# Revit family: Walk_in_Door-ELT_Custom_Coolers-Single_Swing-Left_Hinge
name_source: partatom
category: Doors
units: mm (PartAtom-declared; Revit-internal decimal feet)

## family parameters
Always vertical = Yes
Cut with Voids When Loaded = No
Host = Wall
OmniClass Number = 23.30.10.00
OmniClass Title = Doors
Room Calculation Point = No
Shared = No

## types (18) — shared parameters
Analytic Construction = <None>
Define Thermal Properties by = Schematic Type
Frame Material = ELT_White Stucco Embossed
Frame Width = 5 1/2"
Function = Interior
Manufacturer = ELT Custom Coolers
Panel Material = ELT_White Stucco Embossed
Product Page URL = https://eltcoolerdoors.com
Thickness = 4"
URL = https://eltcoolerdoors.com
Wall Closure = By host

## per-type parameters (varying)
| type | Description | Frame Thickness | Height | Jamb Frame | Model | Plug Frame | Rough Height | Rough Width | Width |
| 72" x 84" Cooler, Jamb Frame | Walk in Swing Cooler Door 72"x 84" Prehung with a Retrofit Heated & Jamb Frame for New Construction. Left Hinge | 1 1/2" | 84" | Yes | ELT 72" x 84" | No | 85" | 71" | 72" |
| 72" x 84" Cooler, Plug Frame | Walk in Swing Cooler Door 72"x 84" Prehung with a Retrofit Heated & Plug Frame for Replacement applications. Left Hinge | 2" | 84" | No | ELT 72" x 84" | Yes | 84" | 69" | 72" |
| 60" x 78" Cooler, Jamb Frame | Walk in Swing Cooler Door 60"x 78" Prehung with a Retrofit Heated & Jamb Frame for New Construction. Left Hinge | 1 1/2" | 78" | Yes | ELT 60" x 78" | No | 79" | 59" | 60" |
| 60" x 78" Cooler, Plug Frame | Walk in Swing Cooler Door 60"x 78" Prehung with a Retrofit Heated & Plug Frame for Replacement applications. Left Hinge | 2" | 78" | No | ELT 60" x 78" | Yes | 78" | 57" | 60" |
| 47" x 78" Cooler, Jamb Frame | Walk in Swing Cooler Door 47"x 78" Prehung with a Retrofit Heated & Jamb Frame for New Construction. Left Hinge | 1 1/2" | 78" | Yes | ELT 47" x 78" | No | 79" | 46" | 47" |
| 47" x 78" Cooler, Plug Frame | Walk in Swing Cooler Door 47"x 78" Prehung with a Retrofit Heated & Plug Frame for Replacement applications. Left Hinge | 2" | 78" | No | ELT 47" x 78" | Yes | 78" | 44" | 47" |
| 47" x 120" Cooler, Jamb Frame | Walk in Swing Cooler Door 47"x 120" Prehung with a Retrofit Heated & Jamb Frame for New Construction. Left Hinge | 1 1/2" | 120" | Yes | ELT 47" x 120" | No | 121" | 46" | 47" |
| 47" x 120" Cooler, Plug Frame | Walk in Swing Cooler Door 47"x 120" Prehung with a Retrofit Heated & Plug Frame for Replacement applications. Left Hinge | 2" | 120" | No | ELT 47" x 120" | Yes | 120" | 44" | 47" |
| 36" x 78" Cooler, Jamb Frame | Walk in Swing Cooler Door 36"x 78" Prehung with a Retrofit Heated & Jamb Frame for New Construction. Left Hinge | 1 1/2" | 78" | Yes | ELT 36" x 78" | No | 79" | 35" | 36" |
| 36" x 78" Cooler, Plug Frame | Walk in Swing Cooler Door 36"x 78" Prehung with a Retrofit Heated & Plug Frame for Replacement applications. Left Hinge | 2" | 78" | No | ELT 36" x 78" | Yes | 78" | 33" | 36" |
| 72" x 84" Freezer, Jamb Frame | Walk in Swing Freezer Door 72"x 84" Prehung with a Retrofit Heated & Jamb Frame for New Construction. Left Hinge | 1 1/2" | 84" | Yes | ELT 72" x 84" | No | 85" | 71" | 72" |
| 72" x 84" Freezer, Plug Frame | Walk in Swing Freezer Door 72"x 84" Prehung with a Retrofit Heated & Plug Frame for Replacement applications. Left Hinge | 2" | 84" | No | ELT 72" x 84" | Yes | 84" | 69" | 72" |
| 60" x 78" Freezer, Jamb Frame | Walk in Swing Freezer Door 60"x 78" Prehung with a Retrofit Heated & Jamb Frame for New Construction. Left Hinge | 1 1/2" | 78" | Yes | ELT 60" x 78" | No | 79" | 59" | 60" |
| 60" x 78" Freezer, Plug Frame | Walk in Swing Freezer Door 60"x 78" Prehung with a Retrofit Heated & Plug Frame for Replacement applications. Left Hinge | 2" | 78" | No | ELT 60" x 78" | Yes | 78" | 57" | 60" |
| 47" x 78" Freezer, Jamb Frame | Walk in Swing Freezer Door 47"x 78" Prehung with a Retrofit Heated & Jamb Frame for New Construction. Left Hinge | 1 1/2" | 78" | Yes | ELT 47" x 78" | No | 79" | 46" | 47" |
| 47" x 78" Freezer, Plug Frame | Walk in Swing Freezer Door 47"x 78" Prehung with a Retrofit Heated & Plug Frame for Replacement applications. Left Hinge | 2" | 78" | No | ELT 47" x 78" | Yes | 78" | 44" | 47" |
| 36" x 78" Freezer, Jamb Frame | Walk in Swing Freezer Door 36"x 78" Prehung with a Retrofit Heated & Jamb Frame for New Construction. Left Hinge | 1 1/2" | 78" | Yes | ELT 36" x 78" | No | 79" | 35" | 36" |
| 36" x 78" Freezer, Plug Frame | Walk in Swing Freezer Door 36"x 78" Prehung with a Retrofit Heated & Plug Frame for Replacement applications. Left Hinge | 2" | 78" | No | ELT 36" x 78" | Yes | 78" | 33" | 36" |

## geometry (parser evidence)
native form markers: Sweep x11
no freeform markers — native parametric forms only
